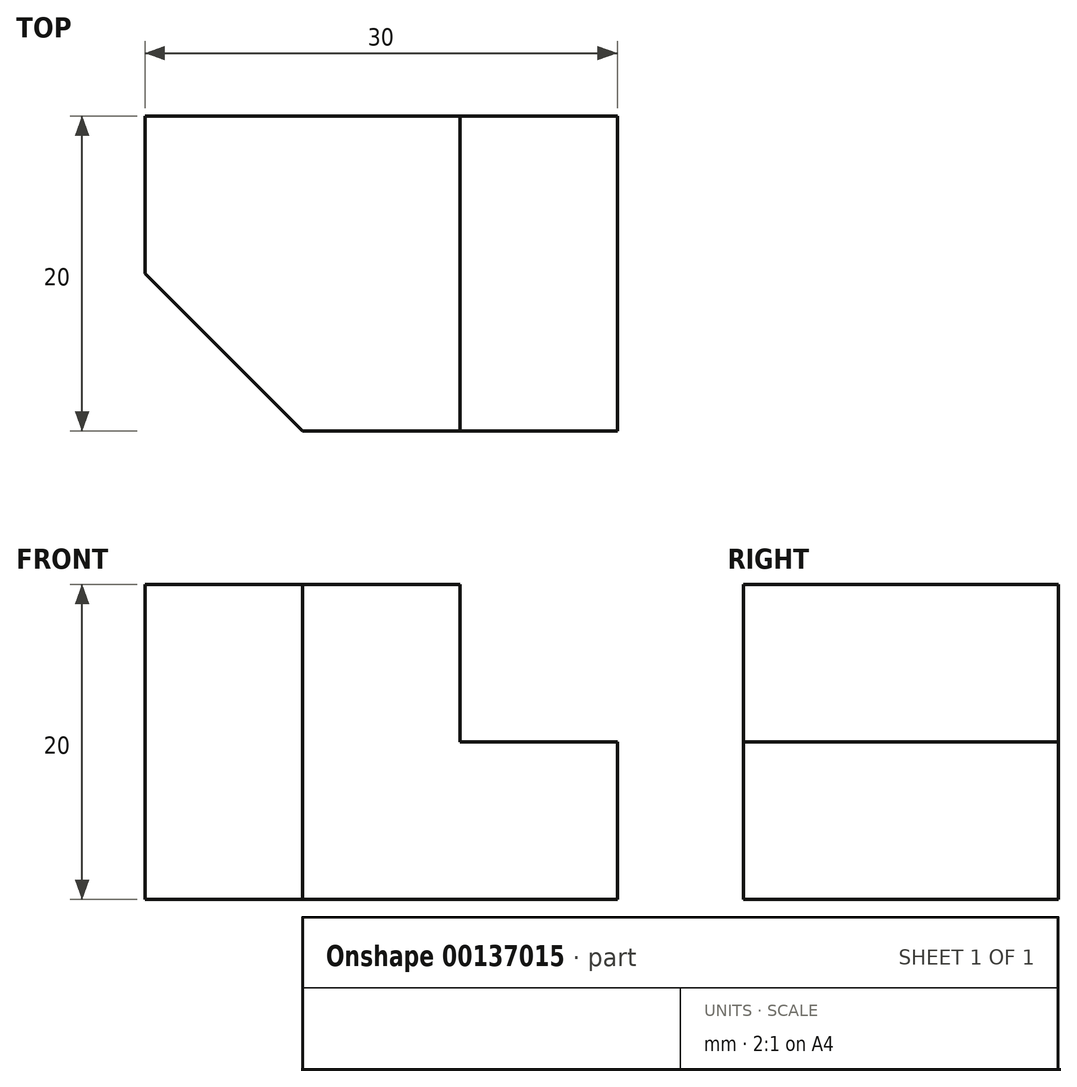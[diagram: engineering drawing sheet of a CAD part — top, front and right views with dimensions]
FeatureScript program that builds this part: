
annotation { "Feature Type Name" : "Feature", "Feature Type Description" : "" }
export const myFeature = defineFeature(function(context is Context, id is Id, definition is map)
    precondition{}
    {
        {
            var Q0;
            Q0=qCreatedBy(makeId("Top.planeOp"),FACE);
            var sketch = newSketch(context, id + "F0", { "sketchPlane" : qUnion([Q0])});
            skLineSegment(sketch, "E0.bottom", {"start": v(0, 0) * mm, "end": v(-30, 0) * mm});
            skLineSegment(sketch, "E0.top", {"start": v(0, -20) * mm, "end": v(-30, -20) * mm});
            skLineSegment(sketch, "E0.left", {"start": v(0, 0) * mm, "end": v(0, -20) * mm});
            skLineSegment(sketch, "E0.right", {"start": v(-30, 0) * mm, "end": v(-30, -20) * mm});
            skSolve(sketch);
        }
        {
            var Q0;
            Q0=makeQuery(id+"F0.imprint","IMPRINT",FACE,{"disambiguationData":[TD([[makeQuery(id+"F0.imprint","IMPRINT",EDGE,{"derivedFrom":sQuery(id+"F0.wireOp",EDGE,"E0.bottom")}),1.0]])]});
            extrude(context, id + "F1", {"entities" : qUnion([Q0]), "depth" : 20 * mm});
        }
        {
            var Q0;
            Q0=makeQuery(id+"F1.opExtrude","CAP_FACE",FACE,{"disambiguationData":[OSD([sQuery(id+"F0.wireOp",EDGE,"E0.bottom"),sQuery(id+"F0.wireOp",EDGE,"E0.top"),sQuery(id+"F0.wireOp",EDGE,"E0.left"),sQuery(id+"F0.wireOp",EDGE,"E0.right")])],"isStart":false});
            var sketch = newSketch(context, id + "F2", { "sketchPlane" : qUnion([Q0])});
            skLineSegment(sketch, "E1", {"start": v(-30, -10) * mm, "end": v(-20, -20) * mm});
            skLineSegment(sketch, "E2", {"start": v(-20, -20) * mm, "end": v(-30, -20) * mm});
            skLineSegment(sketch, "E3", {"start": v(-30, -20) * mm, "end": v(-30, -10) * mm});
            skSolve(sketch);
        }
        {
            var Q0;
            Q0 = qSketchRegion(id + "F2", true);
            extrude(context, id + "F3", {"entities" : qUnion([Q0]), "operationType" : NewBodyOperationType.REMOVE, "endBound" : BoundingType.THROUGH_ALL, "oppositeDirection" : true, "depth" : 25 * mm});
        }
        {
            var Q0;
            Q0=makeQuery(id+"F1.opExtrude","SWEPT_FACE",FACE,{"disambiguationData":[OSD([sQuery(id+"F0.wireOp",EDGE,"E0.top")])]});
            var sketch = newSketch(context, id + "F4", { "sketchPlane" : qUnion([Q0])});
            skPoint(sketch, "E4.oppositeSnap0", {"position": v(0, 10) * mm});
            skPoint(sketch, "E4.oppositeSnap1", {"position": v(-10, 20) * mm});
            skLineSegment(sketch, "E4.bottom", {"start": v(0, 20) * mm, "end": v(-10, 20) * mm});
            skLineSegment(sketch, "E4.top", {"start": v(0, 10) * mm, "end": v(-10, 10) * mm});
            skLineSegment(sketch, "E4.left", {"start": v(0, 20) * mm, "end": v(0, 10) * mm});
            skLineSegment(sketch, "E4.right", {"start": v(-10, 20) * mm, "end": v(-10, 10) * mm});
            skSolve(sketch);
        }
        {
            var Q0;
            Q0=makeQuery(id+"F4.imprint","IMPRINT",FACE,{"disambiguationData":[TD([[makeQuery(id+"F4.imprint","IMPRINT",EDGE,{"derivedFrom":sQuery(id+"F4.wireOp",EDGE,"E4.bottom")}),1.0]])]});
            extrude(context, id + "F5", {"entities" : qUnion([Q0]), "operationType" : NewBodyOperationType.REMOVE, "endBound" : BoundingType.THROUGH_ALL, "oppositeDirection" : true, "depth" : 25 * mm});
        }
    });
